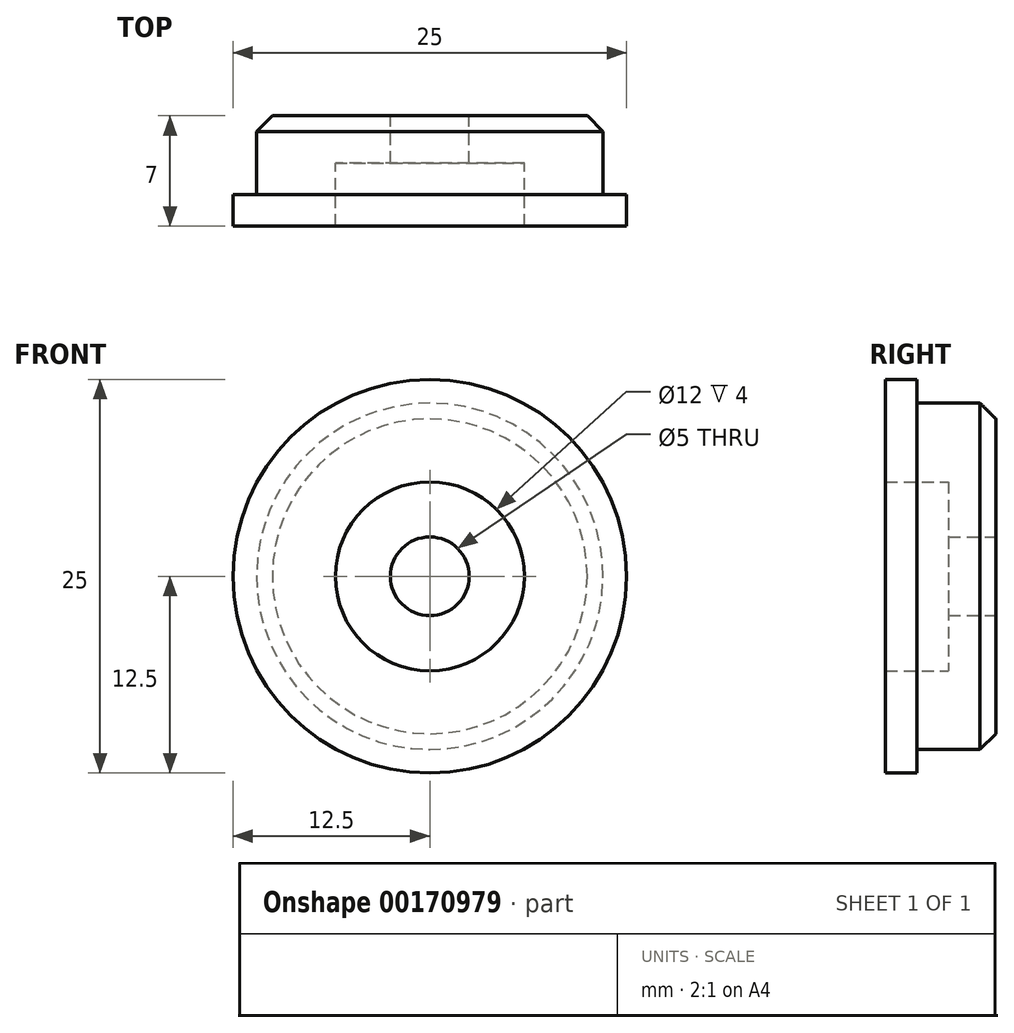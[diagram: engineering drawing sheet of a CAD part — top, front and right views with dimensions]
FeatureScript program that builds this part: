
annotation { "Feature Type Name" : "Feature", "Feature Type Description" : "" }
export const myFeature = defineFeature(function(context is Context, id is Id, definition is map)
    precondition{}
    {
        {
            var Q0;
            Q0=qCreatedBy(makeId("Right.planeOp"),FACE);
            var sketch = newSketch(context, id + "F0", { "sketchPlane" : qUnion([Q0])});
            skLineSegment(sketch, "E0", {"start": v(11.47, 0) * mm, "end": v(0, 0) * mm, "construction": true});
            skLineSegment(sketch, "E1", {"start": v(4, 6) * mm, "end": v(0, 6) * mm});
            skLineSegment(sketch, "E2", {"start": v(4, 2.5) * mm, "end": v(4, 6) * mm});
            skLineSegment(sketch, "E3", {"start": v(7, 2.5) * mm, "end": v(4, 2.5) * mm});
            skLineSegment(sketch, "E4", {"start": v(7, 2.5) * mm, "end": v(7, 11) * mm});
            skLineSegment(sketch, "E5", {"start": v(2, 11) * mm, "end": v(7, 11) * mm});
            skLineSegment(sketch, "E6", {"start": v(2, 11) * mm, "end": v(2, 12.5) * mm});
            skLineSegment(sketch, "E7", {"start": v(0, 12.5) * mm, "end": v(2, 12.5) * mm});
            skLineSegment(sketch, "E8", {"start": v(0, 12.5) * mm, "end": v(0, 6) * mm});
            skSolve(sketch);
        }
        {
            var Q0;
            Q0=makeQuery(id+"F0.imprint","IMPRINT",FACE,{"disambiguationData":[TD([[makeQuery(id+"F0.imprint","IMPRINT",EDGE,{"derivedFrom":sQuery(id+"F0.wireOp",EDGE,"E1")}),-1.0]])]});
            var Q1;
            Q1=sQuery(id+"F0.wireOp",EDGE,"E0");
            revolve(context, id + "F1", {"entities" : qUnion([Q0]), "axis" : qUnion([Q1]), "revolveType" : RevolveType.FULL});
        }
        {
            var Q0;
            Q0=makeQuery(id+"F1.opRevolve","SWEPT_EDGE",EDGE,{"disambiguationData":[OSD([sQuery(id+"F0.wireOp",EDGE,"E4"),sQuery(id+"F0.wireOp",EDGE,"E5")])]});
            chamfer(context, id + "F2", {"entities" : qUnion([Q0]), "width" : 1 * mm, "tangentPropagation" : true});
        }
    });
